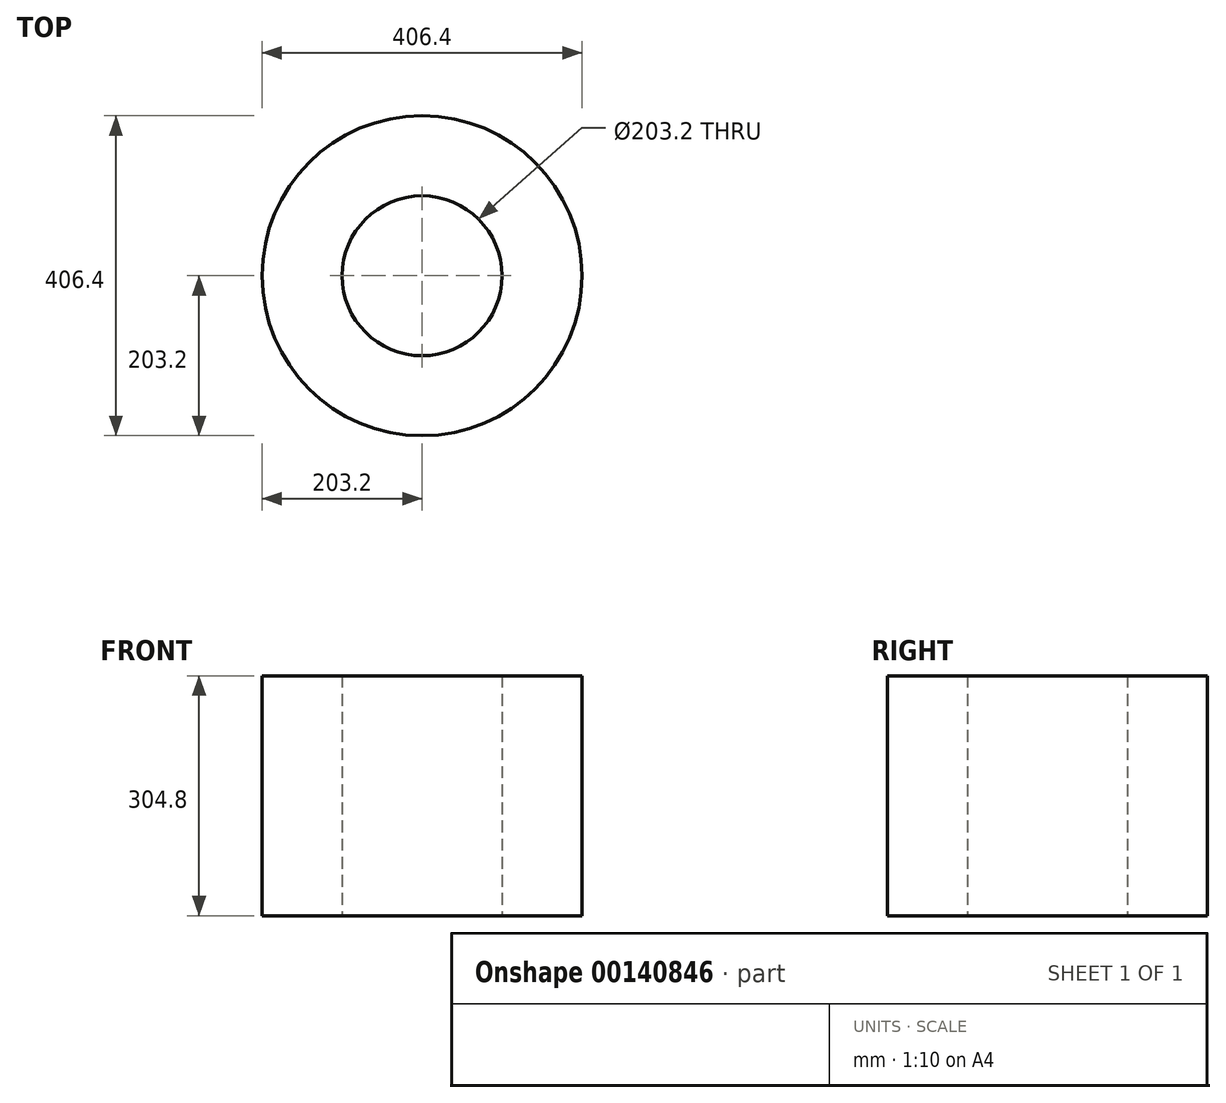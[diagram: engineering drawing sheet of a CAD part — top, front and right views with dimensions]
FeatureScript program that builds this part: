
annotation { "Feature Type Name" : "Feature", "Feature Type Description" : "" }
export const myFeature = defineFeature(function(context is Context, id is Id, definition is map)
    precondition{}
    {
        {
            var Q0;
            Q0=qCreatedBy(makeId("Top.planeOp"),FACE);
            var sketch = newSketch(context, id + "F0", { "sketchPlane" : qUnion([Q0])});
            skCircle(sketch, "E0", {"center": v(0, 0) * mm, "radius": 203.2 * mm});
            skCircle(sketch, "E1", {"center": v(0, 0) * mm, "radius": 101.6 * mm});
            skSolve(sketch);
        }
        {
            var Q0;
            Q0=makeQuery(id+"F0.imprint","IMPRINT",FACE,{"disambiguationData":[TD([[makeQuery(id+"F0.imprint","IMPRINT",EDGE,{"derivedFrom":sQuery(id+"F0.wireOp",EDGE,"E0")}),1.0]])]});
            extrude(context, id + "F1", {"entities" : qUnion([Q0]), "depth" : 304.8 * mm});
        }
    });
